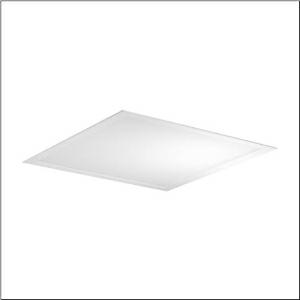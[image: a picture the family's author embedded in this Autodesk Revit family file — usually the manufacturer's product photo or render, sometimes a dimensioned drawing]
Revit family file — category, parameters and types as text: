
# Revit family: apollon_r__31_square_51mp11wd2442_8a23
name_source: partatom
category: Lighting Fixtures
units: mm (PartAtom-declared; Revit-internal decimal feet)

## family parameters
Cut with Voids When Loaded = No
Host = Face
Light Source = No
Part Type = Normal
Room Calculation Point = No
Round Connector Dimension = Use Diameter
Shared = No

## types (1)
- Apollon® 31 square (1 x LED, 4000 lm, 27.5 W, 4000K)
    Apparent Load = 28 VA
    CIE Flux Codes = 61 87 97 100 100
    Color Rendering = 80
    Color Temperature = 4000K
    Default Elevation = 1800 mm
    Description = Apollon® 31 square, office luminaire, primary optical cover: micro prismatic cover, of PMMA, CAT 2 (L<= 3000cd/m²), light emission: direct distribution, primary light characteristic: symmetric, installation type: lay-in mounting, LED, rated luminous flux: 4.000lm, luminous efficacy: 145lm/W, light colour: 840, colour temperature: 4000K, control gear: DALI 2, Multilumen, with terminal, 5-pole, mains connection: 220..240V, AC/DC, 0/50..60Hz, rated input power: 28W, suitable for self-contained emergency lighting element 58DB00B013A with integrated self-test function according to EN 60598-2-22, housing, of aluminium, traffic white (RAL 9016), module: M625, length: 620mm, width: 620mm, height: 62mm, recess depth: 180mm, housing upper side, of sheet steel, coated, protection rating (complete): IP20, protection rating (on room side): IP40, insulation class (complete): insulation class II (safety insulation), certification: CE, ENEC, impact resistance: IK03, permissible operating ambient temperature: -20..+40°C, permissible storage temperature: -20..+60°C, standard: EN 60598-2-22, packaging unit: 1 piece
    Height = 0 mm  [stored 0 ft]
    Lamp = 1 x LED
    Lamp Light Flux = 4000 lm
    Lamp Power = 27.5 W
    Lamp count = 1
    Length = 620 mm
    Luminous efficacy = 145 lm/W
    Manufacturer = Siteco
    ModVariant = No
    Model = 51MP11WD2442
    Mounting Place = Ceiling
    Mounting Type = Recessed
    Number of Poles = 1
    OnlyDefault = Yes
    Power Factor = 1
    Product Name = Apollon® 31 square
    Product group = office luminaire | ceiling recessed
    ProductGroupID = 400
    Protection Class = Protection class II
    Protection Degree = IP 20
    RLX_Detail_Level = 1
    RLX_Emergency_Light_Flux = 0 lm
    RLX_Emergency_Type = 0
    RLX_Emergency_Type_DB = No
    RlxData = <blob elided: 13169 chars, md5=75ed83e1>
    Socket = socket
    Standby Power = 0 W
    System Light Flux = 4000 lm
    System Power = 28 W
    Type Comments = Product without accessories
    Type Image = l_1291039.jpg
    URL = http://relux.com
    VarID = ---
    Voltage = 0 V
    Weight = 0.00 kg
    Width = 620 mm

note: [stored X ft] marks values corroborated as IEEE doubles in the binary element streams (Revit-internal decimal feet)

## geometry (parser evidence)
native form markers: Sweep x10
no freeform markers — native parametric forms only
